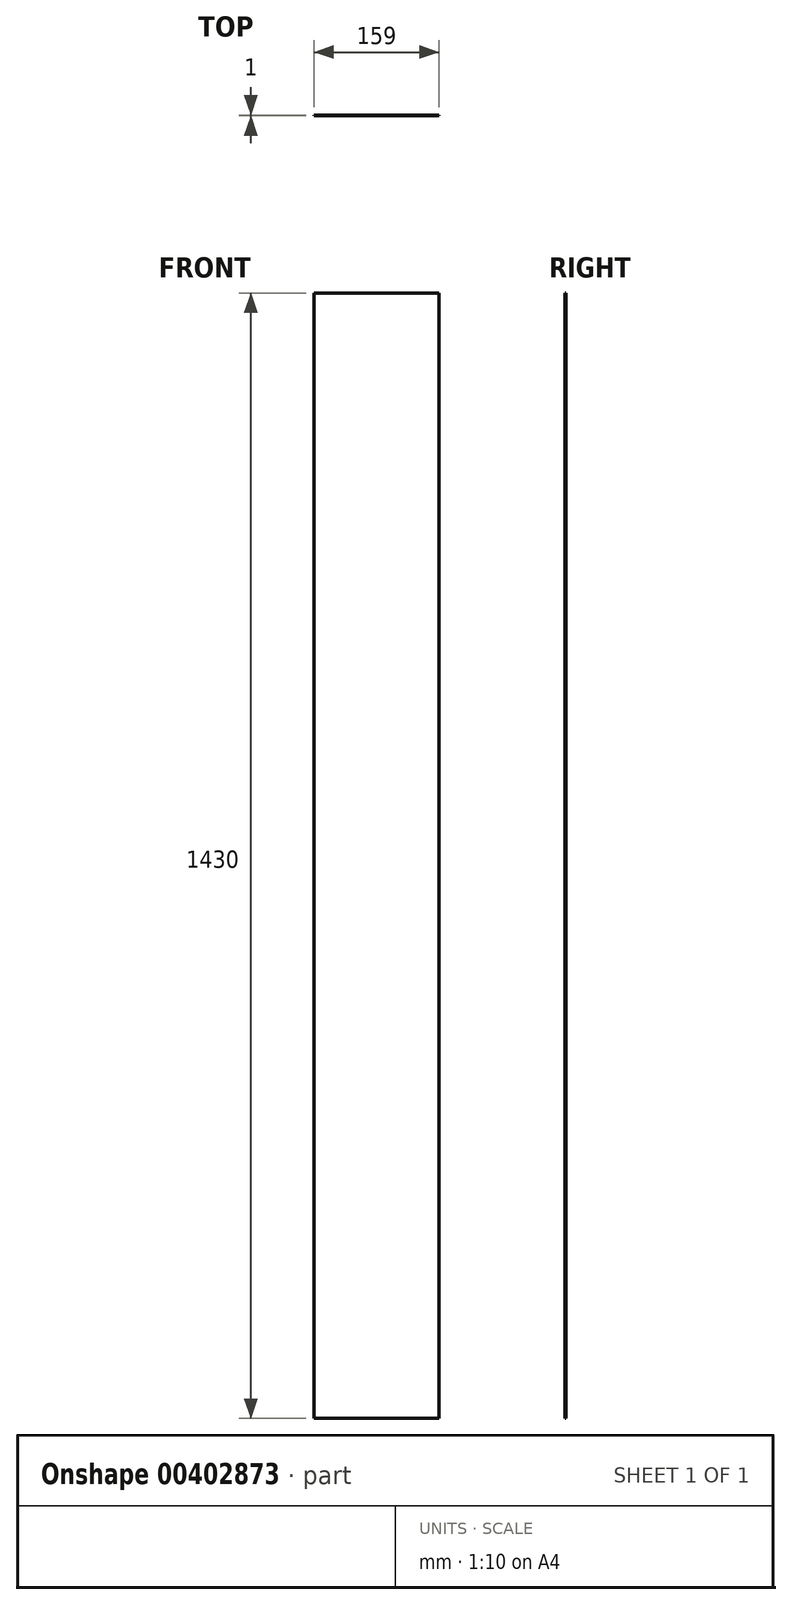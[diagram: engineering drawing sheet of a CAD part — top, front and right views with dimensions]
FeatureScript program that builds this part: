
annotation { "Feature Type Name" : "Feature", "Feature Type Description" : "" }
export const myFeature = defineFeature(function(context is Context, id is Id, definition is map)
    precondition{}
    {
        {
            var Q0;
            Q0=qCreatedBy(makeId("Front.planeOp"),FACE);
            var sketch = newSketch(context, id + "F0", { "sketchPlane" : qUnion([Q0])});
            skLineSegment(sketch, "E0.bottom", {"start": v(-79.5, 715) * mm, "end": v(79.5, 715) * mm});
            skLineSegment(sketch, "E0.top", {"start": v(-79.5, -715) * mm, "end": v(79.5, -715) * mm});
            skLineSegment(sketch, "E0.left", {"start": v(-79.5, 715) * mm, "end": v(-79.5, -715) * mm});
            skLineSegment(sketch, "E0.right", {"start": v(79.5, 715) * mm, "end": v(79.5, -715) * mm});
            skPoint(sketch, "E0.middle", {"position": v(0, 0) * mm});
            skSolve(sketch);
        }
        {
            var Q0;
            Q0=makeQuery(id+"F0.imprint","IMPRINT",FACE,{"disambiguationData":[TD([[makeQuery(id+"F0.imprint","IMPRINT",EDGE,{"derivedFrom":sQuery(id+"F0.wireOp",EDGE,"E0.bottom")}),-1.0]])]});
            extrude(context, id + "F1", {"entities" : qUnion([Q0]), "depth" : 1 * mm});
        }
    });
